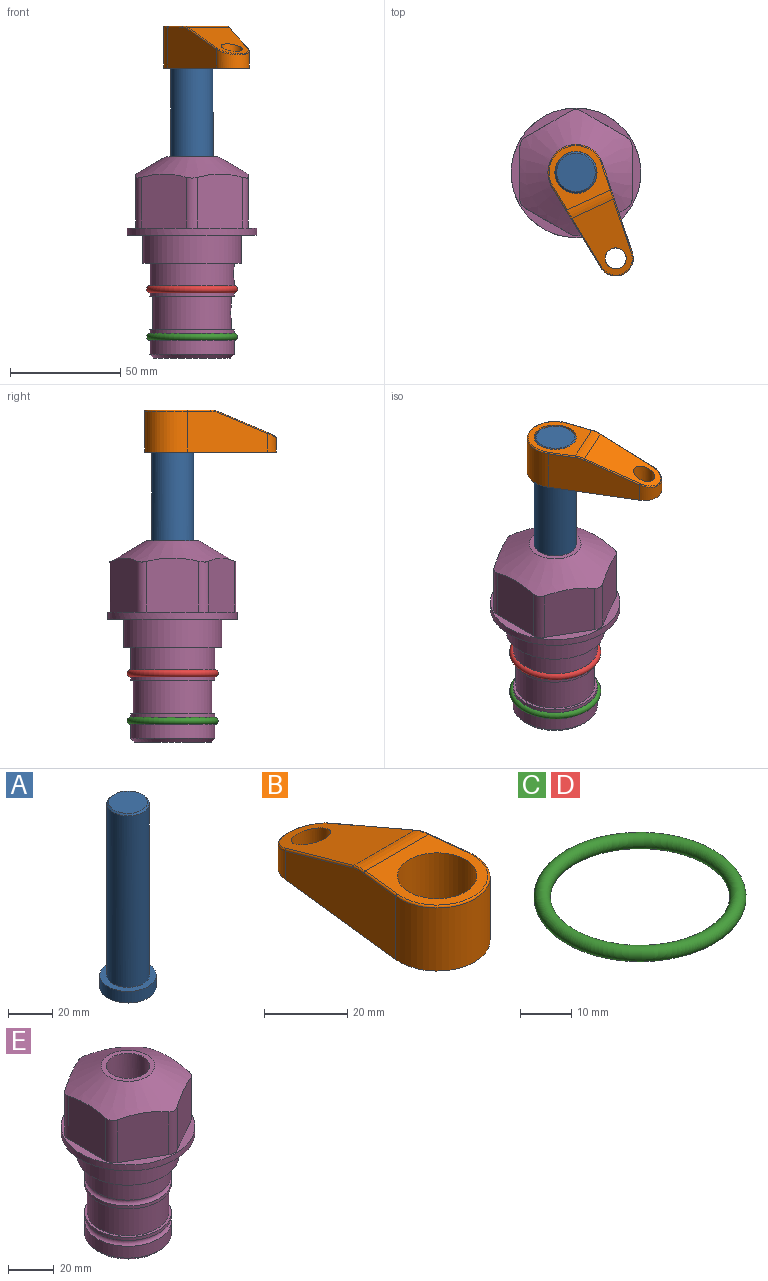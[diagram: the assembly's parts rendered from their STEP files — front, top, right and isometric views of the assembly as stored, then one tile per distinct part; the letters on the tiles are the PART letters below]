
ASSEMBLY  parts=5 mates=3
PART A: 6 faces, bbox 25.4x25.4x101.6 mm
  f0: plane 17.46x17.46mm, normal (0,0,1), area 239.5mm2, adj f5
  f1: plane 25.4x25.4mm, normal (0,0,-1), area 506.7mm2, adj f2
  f2: cylinder r=12.7mm len=25.4mm, axis (0,0,1), area 506.7mm2, adj f1,f3
  f3: plane 25.4x25.4mm, normal (0,0,1), area 221.7mm2, adj f2,f4
  f4: cylinder r=9.53mm len=94.46mm, axis (0,0,1), area 5653mm2, adj f3,f5
  f5: cone r=8.73mm half-angle=45deg, axis (0,0,-1), area 64.4mm2, adj f0,f4
PART B: 44 faces, bbox 27.5x64.5x19.1 mm
  f0: plane 2.3x0.95mm, normal (0,0,-1), area 1mm2, adj f25,f30,f34
  f1: plane 63.5x25.4mm, normal (0,0,-1), area 561.7mm2, adj f2,f3,f4,f5,f6,f7,f19,f20
  f2: cylinder r=12.7mm len=25.4mm, axis (0,0,-1), area 792.2mm2, adj f1,f3,f5,f13
  f3: plane 42.33x18.54mm, normal (0.99,0.11,0), area 647mm2, adj f1,f2,f4,f11,f12,f14
  f4: cylinder r=7.94mm len=15.78mm, axis (0,0,-1), area 158.6mm2, adj f1,f3,f5,f16
  f5: plane 42.33x18.54mm, normal (-0.99,0.11,0), area 647mm2, adj f1,f2,f4,f15,f17,f18
  f6: cylinder r=9.53mm len=19.05mm, axis (0,0,-1), area 1140.1mm2, adj f1,f8
  f7: cylinder r=4.76mm len=10.98mm, axis (0,0,-1), area 276.1mm2, adj f1,f9
  f8: plane 25.83x24.38mm, normal (0,0,1), area 262.2mm2, adj f6,f10,f11,f13,f15
  f9: plane 32.49x20.55mm, normal (0,0.34,0.94), area 489.9mm2, adj f7,f10,f14,f16,f18
  f10: cylinder r=12.7mm len=21.49mm, axis (-1,0,0), area 93.2mm2, adj f8,f9,f12,f17
  f11: cylinder r=0.51mm len=12.34mm, axis (0.11,-0.99,0), area 9.9mm2, adj f3,f8,f12,f13
  f12: bspline ~7.62x1.64mm, area 3.5mm2, adj f3,f10,f11,f14
  f13: torus R=12.19mm, axis (0,0,1), area 33.6mm2, adj f2,f8,f11,f15
  f14: cylinder r=0.51mm len=26.01mm, axis (0.1,-0.93,0.34), area 21.6mm2, adj f3,f9,f12,f16
  f15: cylinder r=0.51mm len=12.34mm, axis (0.11,0.99,0), area 9.9mm2, adj f5,f8,f13,f17
  f16: bspline ~15.78x7.05mm, area 15.7mm2, adj f4,f9,f14,f18
  f17: bspline ~7.62x1.64mm, area 3.5mm2, adj f5,f10,f15,f18
  f18: cylinder r=0.51mm len=26.01mm, axis (0.1,0.93,-0.34), area 21.6mm2, adj f5,f9,f16,f17
  f19: plane 21.6x14.29mm, normal (-0.99,-0.11,0), area 242.6mm2, adj f1,f26,f28,f34,f36,f38
  f20: plane 21.6x14.29mm, normal (0.99,-0.11,0), area 242.6mm2, adj f1,f27,f29,f37,f39,f41
  f21: cylinder r=12.7mm len=14.29mm, axis (0,0,-1), area 173.2mm2, adj f1,f26,f27,f30,f31,f33
  f22: cylinder r=7.94mm len=7.63mm, axis (0,0,-1), area 53.8mm2, adj f1,f28,f29,f42
  f23: plane 2.3x0.95mm, normal (0,0,-1), area 1mm2, adj f25,f33,f37
  f24: plane 17.94x12.32mm, normal (0,-0.34,-0.94), area 191.2mm2, adj f25,f38,f41,f42
  f25: cylinder r=9.53mm len=12.93mm, axis (-1,0,0), area 37.5mm2, adj f0,f23,f24,f31,f36,f39
  f26: cylinder r=1.59mm len=14.29mm, axis (0,0,-1), area 49mm2, adj f1,f19,f21,f32
  f27: cylinder r=1.59mm len=14.29mm, axis (0,0,-1), area 49mm2, adj f1,f20,f21,f35
  f28: cylinder r=1.59mm len=7.28mm, axis (0,0,-1), area 22.1mm2, adj f1,f19,f22,f40
  f29: cylinder r=1.59mm len=7.28mm, axis (0,0,-1), area 22.1mm2, adj f1,f20,f22,f43
  f30: torus R=14.29mm, axis (0,0,1), area 5.8mm2, adj f0,f21,f31,f32
  f31: bspline ~11.06x2.73mm, area 20.8mm2, adj f21,f25,f30,f33
  f32: sphere r=1.59mm, area 5.4mm2, adj f26,f30,f34
  f33: torus R=14.29mm, axis (0,0,1), area 5.8mm2, adj f21,f23,f31,f35
  f34: cylinder r=1.59mm len=1.68mm, axis (-0.11,0.99,0), area 2.4mm2, adj f0,f19,f32,f36
  f35: sphere r=1.59mm, area 5.4mm2, adj f27,f33,f37
  f36: bspline ~5.82x2.33mm, area 7.7mm2, adj f19,f25,f34,f38
  f37: cylinder r=1.59mm len=1.68mm, axis (0.11,0.99,0), area 2.4mm2, adj f20,f23,f35,f39
  f38: cylinder r=1.59mm len=18.33mm, axis (0.1,-0.93,0.34), area 46.7mm2, adj f19,f24,f36,f40
  f39: bspline ~5.82x2.33mm, area 7.7mm2, adj f20,f25,f37,f41
  f40: sphere r=1.59mm, area 3.6mm2, adj f28,f38,f42
  f41: cylinder r=1.59mm len=18.33mm, axis (0.1,0.93,-0.34), area 46.7mm2, adj f20,f24,f39,f43
  f42: bspline ~8.31x1.84mm, area 15.3mm2, adj f22,f24,f40,f43
  f43: sphere r=1.59mm, area 3.6mm2, adj f29,f41,f42
PART C: 1 faces, bbox 44.7x44.7x3.2 mm
  f0: torus R=19.05mm, axis (0,0,1), area 1193.9mm2
PART D: same geometry as C
PART E: 36 faces, bbox 58.7x58.7x91.2 mm
  f0: cylinder r=17.78mm len=35.56mm, axis (0,0,1), area 1670.8mm2, adj f23,f24,f31
  f1: cylinder r=19.05mm len=38.1mm, axis (0,0,1), area 1191.9mm2, adj f26,f27,f30
  f2: plane 58.66x58.66mm, normal (0,0,-1), area 1150.6mm2, adj f3,f28
  f3: cylinder r=29.33mm len=58.66mm, axis (0,0,-1), area 585.1mm2, adj f2,f4
  f4: plane 58.66x58.66mm, normal (0,0,1), area 475.9mm2, adj f3,f5,f6,f7,f8,f9,f10,f11
  f5: plane 24.5x20.32mm, normal (-0.5,0.87,0), area 562.8mm2, adj f4,f15,f16,f17
  f6: plane 24.5x20.32mm, normal (0.5,0.87,0), area 562.8mm2, adj f4,f14,f15,f17
  f7: plane 24.5x23.48mm, normal (1,0,0), area 562.8mm2, adj f4,f13,f14,f17
  f8: plane 24.5x20.32mm, normal (0.5,-0.87,0), area 562.8mm2, adj f4,f12,f13,f17
  f9: plane 24.5x20.32mm, normal (-0.5,-0.87,0), area 562.8mm2, adj f4,f11,f12,f17
  f10: plane 24.5x23.48mm, normal (-1,0,0), area 562.8mm2, adj f4,f11,f16,f17
  f11: cylinder r=5.08mm len=23.01mm, axis (0,0,-1), area 121.2mm2, adj f4,f9,f10,f17
  f12: cylinder r=5.08mm len=23.01mm, axis (0,0,-1), area 121.2mm2, adj f4,f8,f9,f17
  f13: cylinder r=5.08mm len=23.01mm, axis (0,0,-1), area 121.2mm2, adj f4,f7,f8,f17
  f14: cylinder r=5.08mm len=23.01mm, axis (0,0,-1), area 121.2mm2, adj f4,f6,f7,f17
  f15: cylinder r=5.08mm len=23.01mm, axis (0,0,-1), area 121.2mm2, adj f4,f5,f6,f17
  f16: cylinder r=5.08mm len=23.01mm, axis (0,0,-1), area 121.2mm2, adj f4,f5,f10,f17
  f17: cone r=11.73mm half-angle=60deg, axis (0,0,-1), area 2071.8mm2, adj f5,f6,f7,f8,f9,f10,f11,f12
  f18: plane 23.46x23.46mm, normal (0,0,1), area 147.4mm2, adj f17,f35
  f19: plane 34.93x34.93mm, normal (0,0,-1), area 958mm2, adj f29
  f20: cylinder r=19.05mm len=38.1mm, axis (0,0,1), area 760.1mm2, adj f21,f29
  f21: torus R=19.05mm, axis (0,0,1), area 565.3mm2, adj f20,f22
  f22: cylinder r=19.05mm len=38.1mm, axis (0,0,1), area 190mm2, adj f21,f23
  f23: plane 38.1x38.1mm, normal (0,0,1), area 146.9mm2, adj f0,f22
  f24: plane 38.1x38.1mm, normal (0,0,-1), area 146.9mm2, adj f0,f25
  f25: cylinder r=19.05mm len=38.1mm, axis (0,0,1), area 190mm2, adj f24,f26
  f26: torus R=19.05mm, axis (0,0,1), area 565.3mm2, adj f1,f25
  f27: plane 44.45x44.45mm, normal (0,0,-1), area 411.7mm2, adj f1,f28
  f28: cylinder r=22.23mm len=44.45mm, axis (0,0,1), area 1773.5mm2, adj f2,f27
  f29: cone r=19.05mm half-angle=45deg, axis (0,0,1), area 257.5mm2, adj f19,f20
  f30: cylinder r=3.17mm len=6.75mm, axis (-1,0,0), area 128mm2, adj f1,f33
  f31: cylinder r=3.17mm len=6.35mm, axis (-1,0,0), area 102.5mm2, adj f0,f33
  f32: plane 25.4x25.4mm, normal (0,0,1), area 506.7mm2, adj f33
  f33: cylinder r=12.7mm len=66.42mm, axis (0,0,-1), area 5236.2mm2, adj f30,f31,f32,f34
  f34: cone r=9.53mm half-angle=30deg, axis (0,0,-1), area 443.4mm2, adj f33,f35
  f35: cylinder r=9.53mm len=19.05mm, axis (0,0,-1), area 849mm2, adj f18,f34
PLACE A rot(axis=(0,0,-1),65.2deg) t=(0,0,21.02)mm
PLACE B rot(axis=(0,0,-1),155.2deg) t=(0,0,75.63)mm
PLACE C t=(0,0,-21.59)mm
PLACE D at identity
PLACE E at identity fixed
MATE fastened C.f0 <-> E.f0  axis (0,0,1) through (0,0,-46.1)mm
MATE cylindrical A.f2 <-> E.f0  axis (0,0,1) through (0,0,46.66)mm
MATE fastened B.f2 <-> A.f2  axis (0,0,1) through (0,0,94.68)mm
